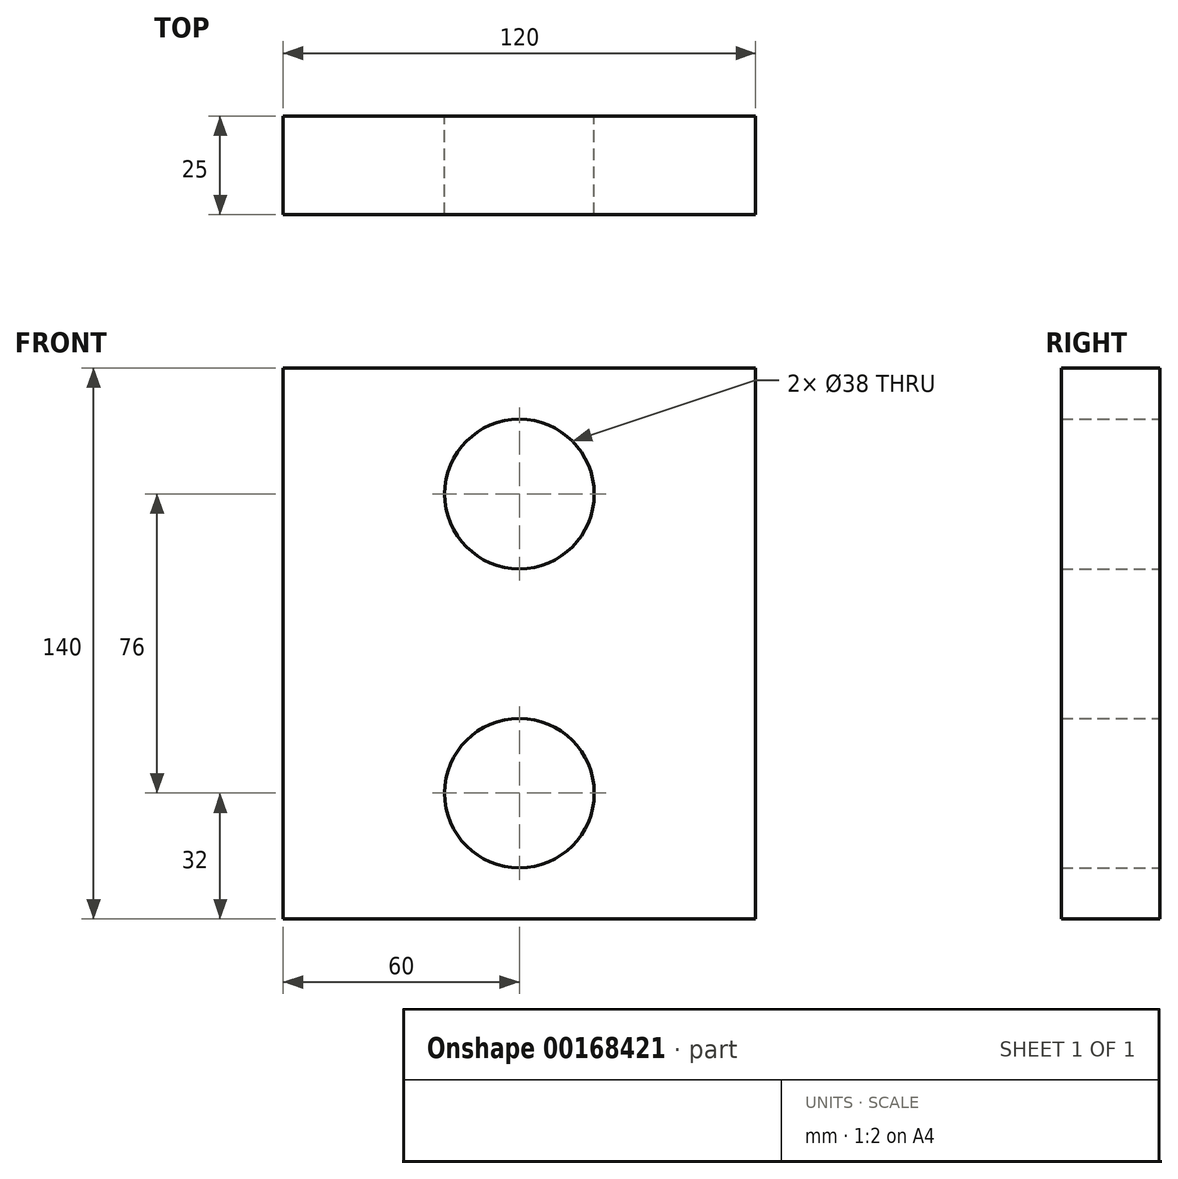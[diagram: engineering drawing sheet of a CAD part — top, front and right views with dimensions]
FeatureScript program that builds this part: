
annotation { "Feature Type Name" : "Feature", "Feature Type Description" : "" }
export const myFeature = defineFeature(function(context is Context, id is Id, definition is map)
    precondition{}
    {
        {
            var Q0;
            Q0=qCreatedBy(makeId("Front.planeOp"),FACE);
            var sketch = newSketch(context, id + "F0", { "sketchPlane" : qUnion([Q0])});
            skLineSegment(sketch, "E0.bottom", {"start": v(60, 70) * mm, "end": v(-60, 70) * mm});
            skLineSegment(sketch, "E0.top", {"start": v(60, -70) * mm, "end": v(-60, -70) * mm});
            skLineSegment(sketch, "E0.left", {"start": v(60, 70) * mm, "end": v(60, -70) * mm});
            skLineSegment(sketch, "E0.right", {"start": v(-60, 70) * mm, "end": v(-60, -70) * mm});
            skPoint(sketch, "E0.middle", {"position": v(0, 0) * mm});
            skLineSegment(sketch, "E1.bottom", {"start": v(60, 19) * mm, "end": v(-60, 19) * mm, "construction": true});
            skLineSegment(sketch, "E1.top", {"start": v(60, -19) * mm, "end": v(-60, -19) * mm, "construction": true});
            skLineSegment(sketch, "E1.left", {"start": v(60, 19) * mm, "end": v(60, -19) * mm, "construction": true});
            skLineSegment(sketch, "E1.right", {"start": v(-60, 17.79) * mm, "end": v(-60, -19) * mm, "construction": true});
            skCircle(sketch, "E2", {"center": v(0, 38) * mm, "radius": 19 * mm});
            skCircle(sketch, "E3", {"center": v(0, -38) * mm, "radius": 19 * mm});
            skSolve(sketch);
        }
        {
            var Q0;
            Q0=qSketchRegion(id+"F0",true);
            extrude(context, id + "F1", {"entities" : qUnion([Q0]), "depth" : 25 * mm});
        }
        {
            var Q0;
            Q0=makeQuery(id+"F0.imprint","IMPRINT",FACE,{"disambiguationData":[TD([[makeQuery(id+"F0.imprint","IMPRINT",EDGE,{"derivedFrom":sQuery(id+"F0.wireOp",EDGE,"E2")}),1.0]])]});
            extrude(context, id + "F2", {"entities" : qUnion([Q0]), "operationType" : NewBodyOperationType.REMOVE, "depth" : 25 * mm});
        }
    });
